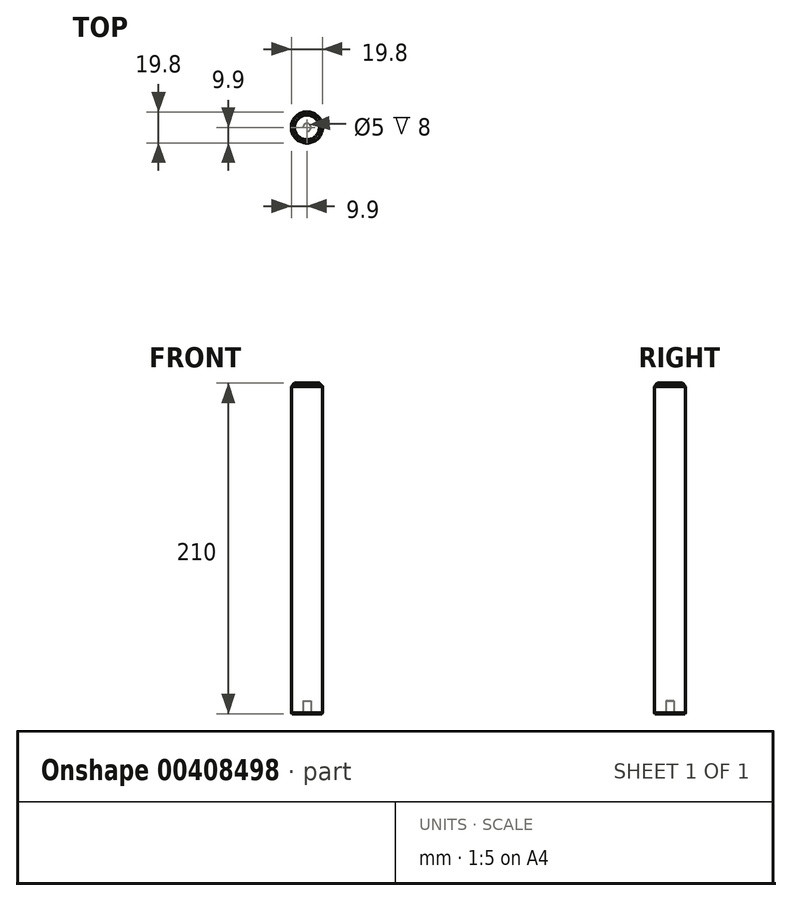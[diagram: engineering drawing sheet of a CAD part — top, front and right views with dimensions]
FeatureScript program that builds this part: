
annotation { "Feature Type Name" : "Feature", "Feature Type Description" : "" }
export const myFeature = defineFeature(function(context is Context, id is Id, definition is map)
    precondition{}
    {
        {
            var Q0;
            Q0=qCreatedBy(makeId("Top.planeOp"),FACE);
            var sketch = newSketch(context, id + "F0", { "sketchPlane" : qUnion([Q0])});
            skCircle(sketch, "E0", {"center": v(0, 0) * mm, "radius": 9.9 * mm});
            skSolve(sketch);
        }
        {
            var Q0;
            Q0 = qSketchRegion(id + "F0", true);
            extrude(context, id + "F1", {"entities" : qUnion([Q0]), "depth" : 210 * mm});
        }
        {
            var Q0;
            Q0=makeQuery(id+"F1.opExtrude","CAP_EDGE",EDGE,{"disambiguationData":[OSD([sQuery(id+"F0.wireOp",EDGE,"E0")])],"isStart":false});
            chamfer(context, id + "F2", {"entities" : qUnion([Q0]), "width" : 2 * mm, "tangentPropagation" : true});
        }
        {
            var Q0;
            Q0=makeQuery(id+"F1.opExtrude","CAP_FACE",FACE,{"disambiguationData":[OSD([sQuery(id+"F0.wireOp",EDGE,"E0")])],"isStart":true});
            var sketch = newSketch(context, id + "F3", { "sketchPlane" : qUnion([Q0])});
            skCircle(sketch, "E1", {"center": v(0, 0) * mm, "radius": 2.5 * mm});
            skSolve(sketch);
        }
        {
            var Q0;
            Q0 = qSketchRegion(id + "F3", true);
            var Q1;
            Q1=makeQuery(id+"F3.imprint","IMPRINT",FACE,{"disambiguationData":[TD([[makeQuery(id+"F3.imprint","IMPRINT",EDGE,{"derivedFrom":sQuery(id+"F3.wireOp",EDGE,"E1")}),1.0]])]});
            extrude(context, id + "F4", {"entities" : qUnion([Q0, Q1]), "operationType" : NewBodyOperationType.REMOVE, "oppositeDirection" : true, "depth" : 8 * mm});
        }
        {
            var Q0;
            Q0=makeQuery(id+"F1.opExtrude","CAP_EDGE",EDGE,{"disambiguationData":[OSD([sQuery(id+"F0.wireOp",EDGE,"E0")])],"isStart":true});
            chamfer(context, id + "F5", {"entities" : qUnion([Q0]), "width" : 0.5 * mm, "tangentPropagation" : true});
        }
    });
